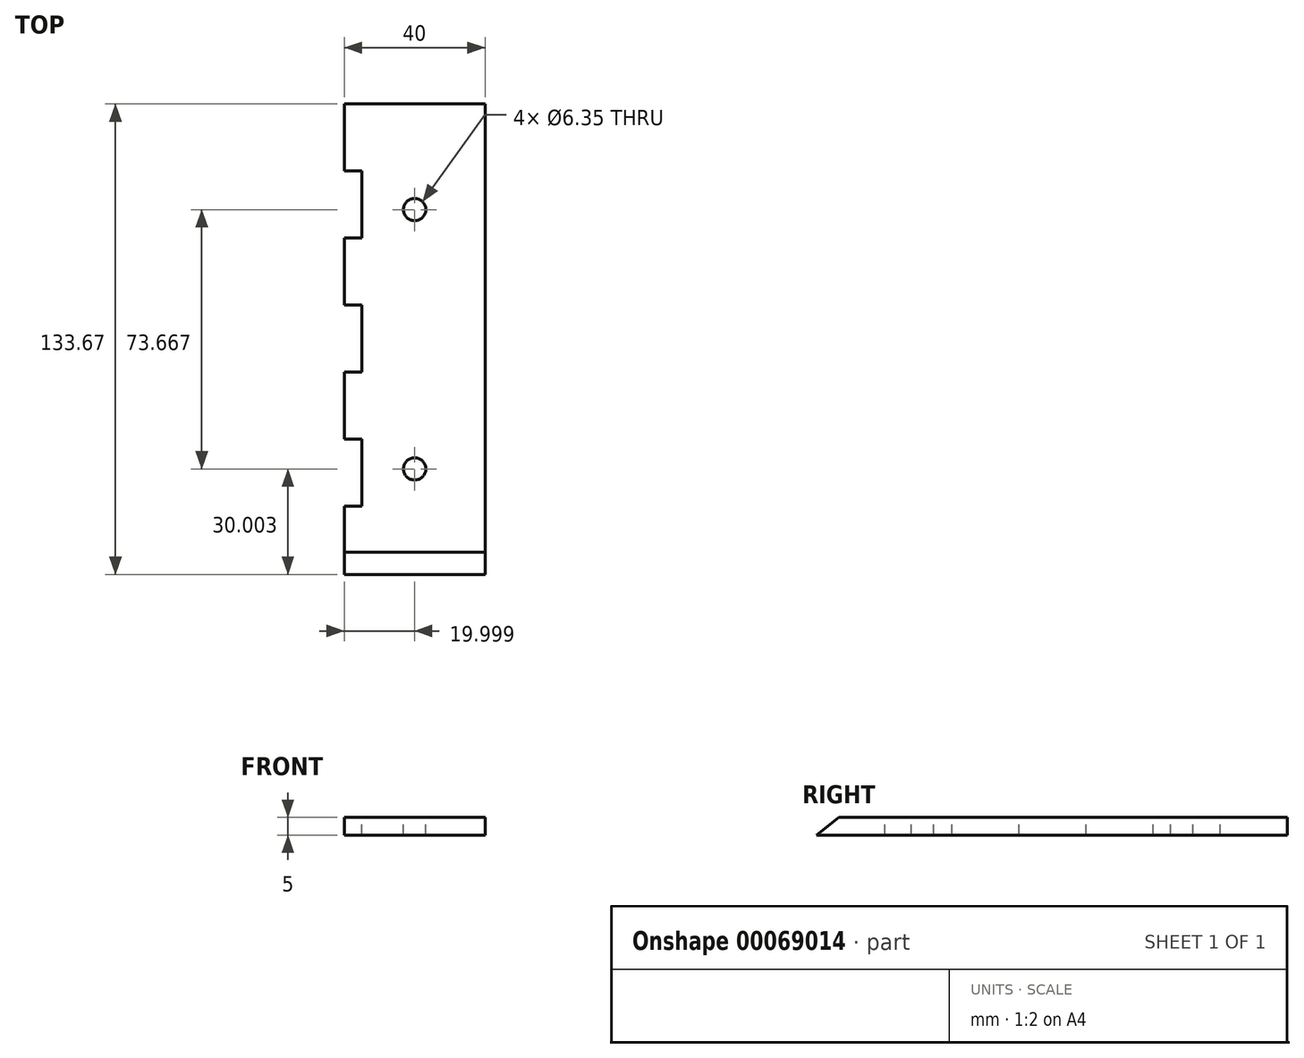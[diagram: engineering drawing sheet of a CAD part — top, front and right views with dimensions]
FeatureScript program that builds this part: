
annotation { "Feature Type Name" : "Feature", "Feature Type Description" : "" }
export const myFeature = defineFeature(function(context is Context, id is Id, definition is map)
    precondition{}
    {
        {
            var Q0;
            Q0=qCreatedBy(makeId("Top.planeOp"),FACE);
            var sketch = newSketch(context, id + "F0", { "sketchPlane" : qUnion([Q0])});
            skLineSegment(sketch, "E0", {"start": v(-54.48, 108.72) * mm, "end": v(-54.48, -24.95) * mm});
            skLineSegment(sketch, "E1", {"start": v(-54.48, 108.72) * mm, "end": v(-14.48, 108.72) * mm});
            skLineSegment(sketch, "E2", {"start": v(-14.48, 108.72) * mm, "end": v(-14.48, -24.95) * mm});
            skLineSegment(sketch, "E3", {"start": v(-14.48, -24.95) * mm, "end": v(-54.48, -24.95) * mm});
            skSolve(sketch);
        }
        {
            var Q0;
            Q0 = qSketchRegion(id + "F0", true);
            extrude(context, id + "F1", {"entities" : qUnion([Q0]), "depth" : 5 * mm});
        }
        {
            var Q0;
            Q0=makeQuery(id+"F1.opExtrude","CAP_FACE",FACE,{"disambiguationData":[OSD([sQuery(id+"F0.wireOp",EDGE,"E0"),sQuery(id+"F0.wireOp",EDGE,"E1"),sQuery(id+"F0.wireOp",EDGE,"E2"),sQuery(id+"F0.wireOp",EDGE,"E3")])],"isStart":false});
            var sketch = newSketch(context, id + "F2", { "sketchPlane" : qUnion([Q0])});
            skPoint(sketch, "E4", {"position": v(-54.48, 89.67) * mm});
            skPoint(sketch, "E5", {"position": v(-54.48, 70.62) * mm});
            skPoint(sketch, "E6", {"position": v(-54.48, 51.57) * mm});
            skPoint(sketch, "E7", {"position": v(-54.48, 32.52) * mm});
            skPoint(sketch, "E8", {"position": v(-54.48, 13.47) * mm});
            skPoint(sketch, "E9", {"position": v(-54.48, -9.12) * mm});
            skPoint(sketch, "E10", {"position": v(-54.48, -5.58) * mm});
            skPoint(sketch, "E11", {"position": v(-54.48, 108.72) * mm});
            skLineSegment(sketch, "E12.bottom", {"start": v(-54.48, 108.72) * mm, "end": v(-49.48, 108.72) * mm});
            skLineSegment(sketch, "E12.top", {"start": v(-54.48, 89.67) * mm, "end": v(-49.48, 89.67) * mm});
            skLineSegment(sketch, "E12.left", {"start": v(-54.48, 108.72) * mm, "end": v(-54.48, 89.67) * mm});
            skLineSegment(sketch, "E12.right", {"start": v(-49.48, 108.72) * mm, "end": v(-49.48, 89.67) * mm});
            skLineSegment(sketch, "E13", {"start": v(-54.48, 108.72) * mm, "end": v(-54.48, -24.95) * mm, "construction": true});
            skLineSegment(sketch, "E14.bottom", {"start": v(-54.48, 70.62) * mm, "end": v(-49.48, 70.62) * mm});
            skLineSegment(sketch, "E14.top", {"start": v(-54.48, 51.57) * mm, "end": v(-49.48, 51.57) * mm});
            skLineSegment(sketch, "E14.left", {"start": v(-54.48, 70.62) * mm, "end": v(-54.48, 51.57) * mm});
            skLineSegment(sketch, "E14.right", {"start": v(-49.48, 70.62) * mm, "end": v(-49.48, 51.57) * mm});
            skLineSegment(sketch, "E15.bottom", {"start": v(-54.48, 32.52) * mm, "end": v(-49.48, 32.52) * mm});
            skLineSegment(sketch, "E15.top", {"start": v(-54.48, 13.47) * mm, "end": v(-49.48, 13.47) * mm});
            skLineSegment(sketch, "E15.left", {"start": v(-54.48, 32.52) * mm, "end": v(-54.48, 13.47) * mm});
            skLineSegment(sketch, "E15.right", {"start": v(-49.48, 32.52) * mm, "end": v(-49.48, 13.47) * mm});
            skLineSegment(sketch, "E16.bottom", {"start": v(-54.48, -5.58) * mm, "end": v(-49.48, -5.58) * mm});
            skLineSegment(sketch, "E16.top", {"start": v(-54.48, -24.95) * mm, "end": v(-49.48, -24.95) * mm});
            skLineSegment(sketch, "E16.left", {"start": v(-54.48, -5.58) * mm, "end": v(-54.48, -24.95) * mm});
            skLineSegment(sketch, "E16.right", {"start": v(-49.48, -5.58) * mm, "end": v(-49.48, -24.95) * mm});
            skLineSegment(sketch, "E17", {"start": v(-49.48, 108.72) * mm, "end": v(-49.48, -24.95) * mm});
            skLineSegment(sketch, "E18", {"start": v(-54.48, -24.95) * mm, "end": v(-54.48, 13.47) * mm});
            skLineSegment(sketch, "E19", {"start": v(-54.48, -24.95) * mm, "end": v(-54.48, 108.72) * mm});
            skSolve(sketch);
        }
        {
            var Q0;
            {var subQ0=sQuery(id+"F2.wireOp",EDGE,"E12.top");Q0=makeQuery(id+"F2.imprint","IMPRINT",FACE,{"disambiguationData":[TD([[makeQuery(id+"F2.imprint","IMPRINT",EDGE,{"derivedFrom":subQ0}),-1.0]])]});}
            var Q1;
            {var subQ0=sQuery(id+"F2.wireOp",EDGE,"E14.top");Q1=makeQuery(id+"F2.imprint","IMPRINT",FACE,{"disambiguationData":[TD([[makeQuery(id+"F2.imprint","IMPRINT",EDGE,{"derivedFrom":subQ0}),-1.0]])]});}
            var Q2;
            {var subQ0=sQuery(id+"F2.wireOp",EDGE,"E15.top");Q2=makeQuery(id+"F2.imprint","IMPRINT",FACE,{"disambiguationData":[TD([[makeQuery(id+"F2.imprint","IMPRINT",EDGE,{"derivedFrom":subQ0}),-1.0]])]});}
            extrude(context, id + "F3", {"entities" : qUnion([Q0, Q1, Q2]), "operationType" : NewBodyOperationType.REMOVE, "oppositeDirection" : true, "depth" : 25.4 * mm});
        }
        {
            var Q0;
            Q0=makeQuery(id+"F1.opExtrude","SWEPT_FACE",FACE,{"disambiguationData":[OSD([sQuery(id+"F0.wireOp",EDGE,"E2")])]});
            var sketch = newSketch(context, id + "F4", { "sketchPlane" : qUnion([Q0])});
            skLineSegment(sketch, "E20", {"start": v(-24.95, 0) * mm, "end": v(-18.6, 5) * mm});
            skSolve(sketch);
        }
        {
            var Q0;
            Q0 = qSketchRegion(id + "F4", true);
            var Q1;
            {var subQ0=sQuery(id+"F4.wireOp",EDGE,"7dLSJror-Nn6T-6Vtq-xXIe-voesyWZ8YN49");Q1=makeQuery(id+"F4.imprint","IMPRINT",FACE,{"disambiguationData":[TD([[makeQuery(id+"F4.imprint","IMPRINT",EDGE,{"derivedFrom":subQ0}),1.0]])]});}
            var Q2;
            {var subQ0=sQuery(id+"F4.wireOp",EDGE,"E20");Q2=makeQuery(id+"F4.imprint","IMPRINT",FACE,{"disambiguationData":[TD([[makeQuery(id+"F4.imprint","IMPRINT",EDGE,{"derivedFrom":subQ0}),1.0]])]});}
            extrude(context, id + "F5", {"entities" : qUnion([Q0, Q1, Q2]), "operationType" : NewBodyOperationType.REMOVE, "endBound" : BoundingType.THROUGH_ALL, "oppositeDirection" : true, "depth" : 25.4 * mm});
        }
        {
            var Q0;
            Q0=makeQuery(id+"F1.opExtrude","CAP_FACE",FACE,{"disambiguationData":[OSD([sQuery(id+"F0.wireOp",EDGE,"E0"),sQuery(id+"F0.wireOp",EDGE,"E1"),sQuery(id+"F0.wireOp",EDGE,"E2"),sQuery(id+"F0.wireOp",EDGE,"E3")])],"isStart":false});
            var sketch = newSketch(context, id + "F6", { "sketchPlane" : qUnion([Q0])});
            skPoint(sketch, "E21", {"position": v(-34.48, 78.72) * mm});
            skPoint(sketch, "E22", {"position": v(-34.48, 5.05) * mm});
            skCircle(sketch, "E23", {"center": v(-34.48, 5.05) * mm, "radius": 3.18 * mm});
            skCircle(sketch, "E24", {"center": v(-34.48, 78.72) * mm, "radius": 3.18 * mm});
            skSolve(sketch);
        }
        {
            var Q0;
            Q0 = qSketchRegion(id + "F6", true);
            extrude(context, id + "F7", {"entities" : qUnion([Q0]), "operationType" : NewBodyOperationType.REMOVE, "oppositeDirection" : true, "depth" : 25.4 * mm});
        }
        {
            var Q0;
            Q0=makeQuery(id+"F1.opExtrude","SWEPT_BODY",BODY,{"disambiguationData":[OSD([sQuery(id+"F0.wireOp",EDGE,"E0"),sQuery(id+"F0.wireOp",EDGE,"E1"),sQuery(id+"F0.wireOp",EDGE,"E2"),sQuery(id+"F0.wireOp",EDGE,"E3")])]});
            transform(context, id + "F8", {"entities" : qUnion([Q0]), "transformType" : TransformType.TRANSLATION_3D, "dx" : 0 * mm, "dy" : 0 * mm, "dz" : 0 * mm, "makeCopy" : true});
        }
    });
